# Revit family: Grohe_ConcealedShowerSystemWithRainshowerMono310Cube_34865KF0
name_source: partatom
category: Plumbing Fixtures
units: mm (PartAtom-declared; Revit-internal decimal feet)

## family parameters
Cut with Voids When Loaded = No
Host = Face
OmniClass Number = 23.45.05.00
OmniClass Title = Sanitary Equipment
Part Type = Normal
Room Calculation Point = No
Round Connector Dimension = Use Diameter
Shared = No

## types (1)
- Concealed Shower System With Rainshower Mono 310 Cube (34865KF0)
    Assembly Code = D2013
    AssetType = Fixed
    BIMObjectName = Grohe_ConcealedShowerSystemWithRainshowerMono310Cube_34865KF0
    CO2NeutralProduction = GROHE is one of the first leading manufacturer within the sanitary industry having a CO2-neutral production.
    ClassificationName = Uniclass2015
    ClassificationValue = Pr_40_20_87_55
    Color = Grohe_Black
    Cost = 0 $
    Default Elevation = 0 mm  [stored 0 ft]
    Description = Concealed Shower System With Rainshower Mono 310 Cube
    DimensionsDocumentLink = https://cdn.cloud.grohe.com
    DocumentationCertificates = https://www.bimstore.co
    DocumentationInstallationGuide = https://www.bimstore.co
    DocumentationLiterature = https://www.bimstore.co
    DocumentationMaintenance = https://www.bimstore.co
    DocumentationTechnical = https://www.bimstore.co
    DurationUnit = Years
    Ecojoy = No
    ExpectedLife = 0
    Finish = Black
    FullRecyclabilityOfPlastic = All plastic components are fully recycable
    GROHESocialCommittment = green.grohe.com/social_engagement
    GROHESustainability = green.grohe.com
    IfcExportAs = IfcPipeFitting
    IfcExportType = IfcPipeFittingType
    Keynote = N16
    Manufacturer = Grohe
    ManufacturerName = Grohe
    Model = Concealed Shower System With Rainshower Mono 310 Cube
    ModelNumber = 34865KF0
    ModelReference = Concealed Shower System With Rainshower Mono 310 Cube
    NBSDescription = Shower fittings package
    NBSObjectName = Grohe - Shower fittings package
    NBSReference = 45-35-70/326
    NominalDepth = 0 mm  [stored 0 ft]
    NominalHeight = 0 mm  [stored 0 ft]
    NominalLength = 0 mm  [stored 0 ft]
    PrimaryMaterial = Grohe_Black
    ProductDescription = consisting of:

concealed thermostat with 2 valves and integrated hand shower holder

GROHE Rapido SmartBox universal rough-in box, 1/2" (35 604)

Rainshower Mono Cube 310 head shower set including horizontal shower arm 422 mm

Rainshower SmartActive 130 Cube hand shower 3 sprays

Silverflex shower hose 1500 mm 1/2" x 1/2"

optional flow regulator 9.5 l/min included for hand shower and head shower
    ProductNumber = 34865KF0
    ProductShortText = Concealed shower system with Rainshower Mono 310 Cube
    ProductType = Thermostat
    ProductionYear = 2023
    SustainabilityAward = green.grohe.com/awards
    SustainabilityReport = green.grohe.com/reporting
    Type Comments = Concealed Shower System With Rainshower Mono 310 Cube
    TypeName = Concealed Shower System With Rainshower Mono 310 Cube
    URL = https://www.grohe.co.uk
    WarrantyDurationLabor = 0
    WarrantyDurationParts = 0
    WarrantyDurationUnit = Years
    _BSBibleVersion = 17
    _BimSpecGuid = 0
    _CurrentRevision = 1
    _DistributedBy = https://www.bimstore.co
    _ObjectUserGuide = https://www.bimstore.co

note: [stored X ft] marks values corroborated as IEEE doubles in the binary element streams (Revit-internal decimal feet)

## geometry (parser evidence)
native form markers: Sweep x2
no freeform markers — native parametric forms only
